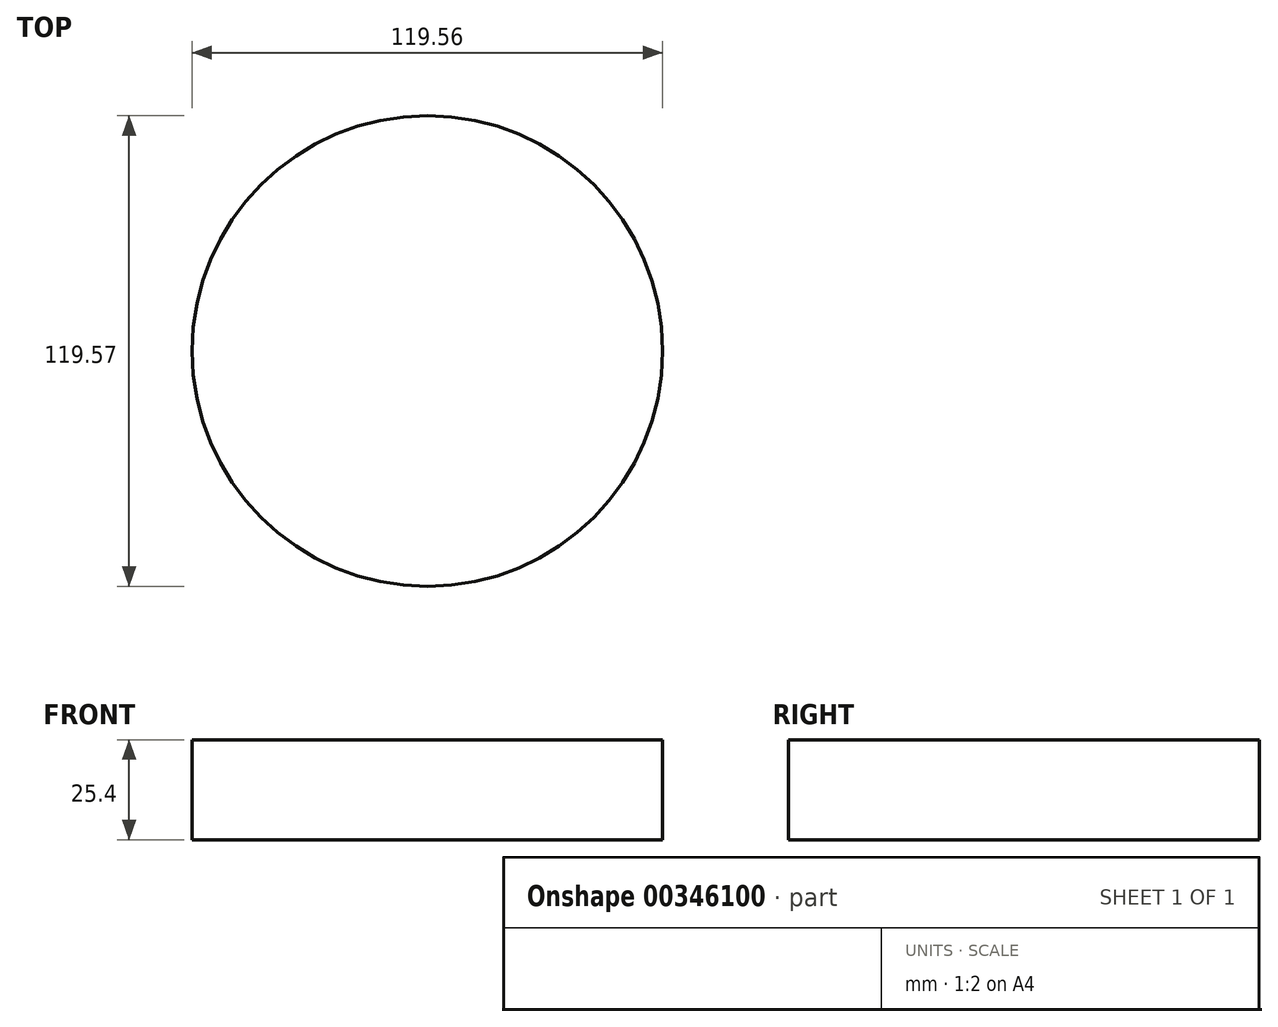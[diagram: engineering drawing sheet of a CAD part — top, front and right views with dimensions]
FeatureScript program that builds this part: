
annotation { "Feature Type Name" : "Feature", "Feature Type Description" : "" }
export const myFeature = defineFeature(function(context is Context, id is Id, definition is map)
    precondition{}
    {
        {
            var Q0;
            Q0=qCreatedBy(makeId("Top.planeOp"),FACE);
            var sketch = newSketch(context, id + "F0", { "sketchPlane" : qUnion([Q0])});
            skCircle(sketch, "E0", {"center": v(-125.9, 13.49) * mm, "radius": 59.78 * mm});
            skSolve(sketch);
        }
        {
            var Q0;
            Q0 = qSketchRegion(id + "F0", true);
            extrude(context, id + "F1", {"entities" : qUnion([Q0]), "depth" : 25.4 * mm});
        }
    });
